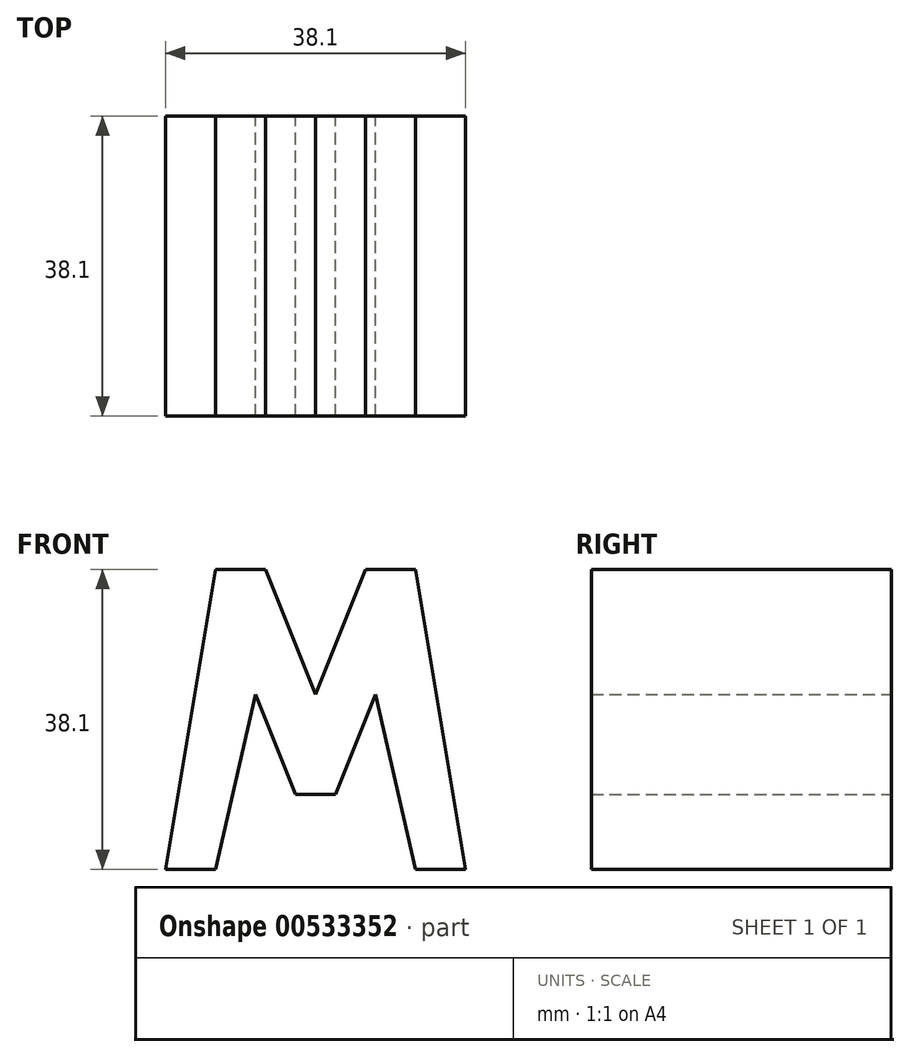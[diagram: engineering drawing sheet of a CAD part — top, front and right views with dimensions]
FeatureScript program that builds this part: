
annotation { "Feature Type Name" : "Feature", "Feature Type Description" : "" }
export const myFeature = defineFeature(function(context is Context, id is Id, definition is map)
    precondition{}
    {
        {
            var Q0;
            Q0=qCreatedBy(makeId("Front.planeOp"),FACE);
            cPlane(context, id + "F0", {"entities" : qUnion([Q0]), "cplaneType" : CPlaneType.OFFSET, "offset" : 38.1 * mm, "width" : 152.4 * mm, "height" : 152.4 * mm});
        }
        {
            var Q0;
            Q0=qCreatedBy(id+"F0.planeOp",FACE);
            var sketch = newSketch(context, id + "F1", { "sketchPlane" : qUnion([Q0])});
            skLineSegment(sketch, "E0", {"start": v(0, 0) * mm, "end": v(0, 38.1) * mm});
            skLineSegment(sketch, "E1", {"start": v(0, 38.1) * mm, "end": v(38.1, 38.1) * mm});
            skLineSegment(sketch, "E2", {"start": v(38.1, 38.1) * mm, "end": v(38.1, 0) * mm});
            skLineSegment(sketch, "E3", {"start": v(38.1, 0) * mm, "end": v(0, 0) * mm});
            skLineSegment(sketch, "E4", {"start": v(0, 0) * mm, "end": v(6.35, 38.1) * mm});
            skLineSegment(sketch, "E5", {"start": v(6.35, 38.1) * mm, "end": v(12.7, 38.1) * mm});
            skLineSegment(sketch, "E6", {"start": v(12.7, 38.1) * mm, "end": v(19.05, 22.23) * mm});
            skLineSegment(sketch, "E7", {"start": v(19.05, 22.22) * mm, "end": v(25.4, 38.1) * mm});
            skLineSegment(sketch, "E8", {"start": v(25.4, 38.1) * mm, "end": v(31.75, 38.1) * mm});
            skLineSegment(sketch, "E9", {"start": v(31.75, 38.1) * mm, "end": v(38.1, 0) * mm});
            skLineSegment(sketch, "E10", {"start": v(0, 0) * mm, "end": v(6.35, 0) * mm});
            skLineSegment(sketch, "E11", {"start": v(6.35, 0) * mm, "end": v(0, 0) * mm});
            skLineSegment(sketch, "E12", {"start": v(6.35, 0) * mm, "end": v(11.43, 22.23) * mm});
            skLineSegment(sketch, "E13", {"start": v(31.75, 0) * mm, "end": v(38.1, 0) * mm});
            skLineSegment(sketch, "E14", {"start": v(11.43, 22.23) * mm, "end": v(16.5, 9.52) * mm});
            skLineSegment(sketch, "E15", {"start": v(26.67, 22.23) * mm, "end": v(21.59, 9.53) * mm});
            skLineSegment(sketch, "E16", {"start": v(21.59, 9.52) * mm, "end": v(16.5, 9.52) * mm});
            skLineSegment(sketch, "E17", {"start": v(26.67, 22.23) * mm, "end": v(31.75, 0) * mm});
            skSolve(sketch);
        }
        {
            var Q0;
            Q0=makeQuery(id+"F1.imprint","IMPRINT",FACE,{"disambiguationData":[TD([[makeQuery(id+"F1.imprint","IMPRINT",EDGE,{"derivedFrom":sQuery(id+"F1.wireOp",EDGE,"E4")}),-1.0]])]});
            extrude(context, id + "F2", {"entities" : qUnion([Q0]), "depth" : 38.1 * mm, "offsetDistance" : 25.4 * mm});
        }
    });
